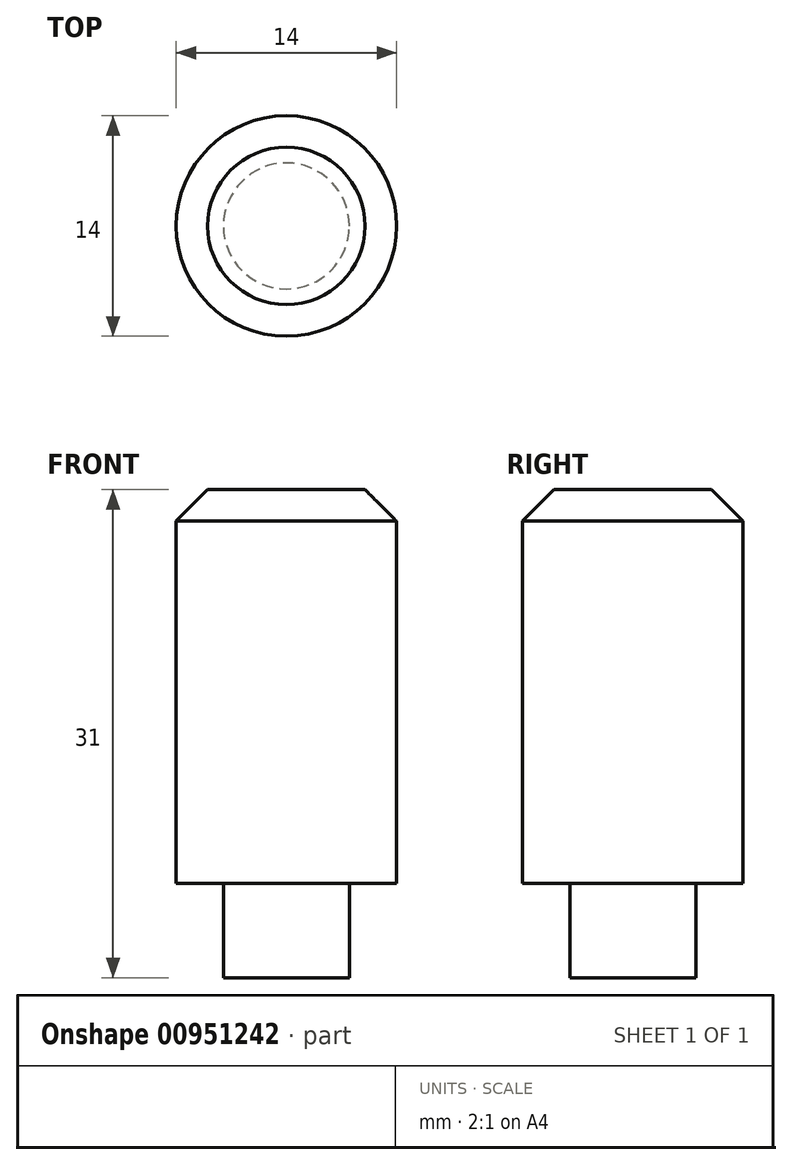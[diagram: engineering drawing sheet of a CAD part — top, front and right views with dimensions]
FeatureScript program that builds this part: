
annotation { "Feature Type Name" : "Feature", "Feature Type Description" : "" }
export const myFeature = defineFeature(function(context is Context, id is Id, definition is map)
    precondition{}
    {
        {
            var Q0;
            Q0=qCreatedBy(makeId("Top.planeOp"),FACE);
            var sketch = newSketch(context, id + "F0", { "sketchPlane" : qUnion([Q0])});
            skCircle(sketch, "E0", {"center": v(0, 0) * mm, "radius": 4 * mm});
            skSolve(sketch);
        }
        {
            var Q0;
            Q0=makeQuery(id+"F0.imprint","IMPRINT",FACE,{"disambiguationData":[TD([[makeQuery(id+"F0.imprint","IMPRINT",EDGE,{"derivedFrom":sQuery(id+"F0.wireOp",EDGE,"E0")}),1.0]])]});
            extrude(context, id + "F1", {"entities" : qUnion([Q0]), "depth" : 6 * mm, "offsetDistance" : 25 * mm});
        }
        {
            var Q0;
            Q0=makeQuery(id+"F1.opExtrude","CAP_FACE",FACE,{"disambiguationData":[OSD([sQuery(id+"F0.wireOp",EDGE,"E0")])],"isStart":false});
            var sketch = newSketch(context, id + "F2", { "sketchPlane" : qUnion([Q0])});
            skCircle(sketch, "E1", {"center": v(0, 0) * mm, "radius": 7 * mm});
            skSolve(sketch);
        }
        {
            var Q0;
            Q0=makeQuery(id+"F2.imprint","IMPRINT",FACE,{"disambiguationData":[TD([[makeQuery(id+"F2.imprint","IMPRINT",EDGE,{"derivedFrom":makeQuery(id+"F1.opExtrude","CAP_EDGE",EDGE,{"disambiguationData":[OSD([sQuery(id+"F0.wireOp",EDGE,"E0")])],"isStart":false})}),1.0]])]});
            var Q1;
            Q1=makeQuery(id+"F2.imprint","IMPRINT",FACE,{"disambiguationData":[TD([[makeQuery(id+"F2.imprint","IMPRINT",EDGE,{"derivedFrom":sQuery(id+"F2.wireOp",EDGE,"E1")}),1.0]])]});
            extrude(context, id + "F3", {"entities" : qUnion([Q0, Q1]), "operationType" : NewBodyOperationType.ADD, "depth" : 25 * mm, "offsetDistance" : 25 * mm});
        }
        {
            var Q0;
            Q0=makeQuery(id+"F3.opExtrude","CAP_EDGE",EDGE,{"disambiguationData":[OSD([sQuery(id+"F2.wireOp",EDGE,"E1")])],"isStart":false});
            chamfer(context, id + "F4", {"entities" : qUnion([Q0]), "width" : 2 * mm, "tangentPropagation" : true});
        }
    });
